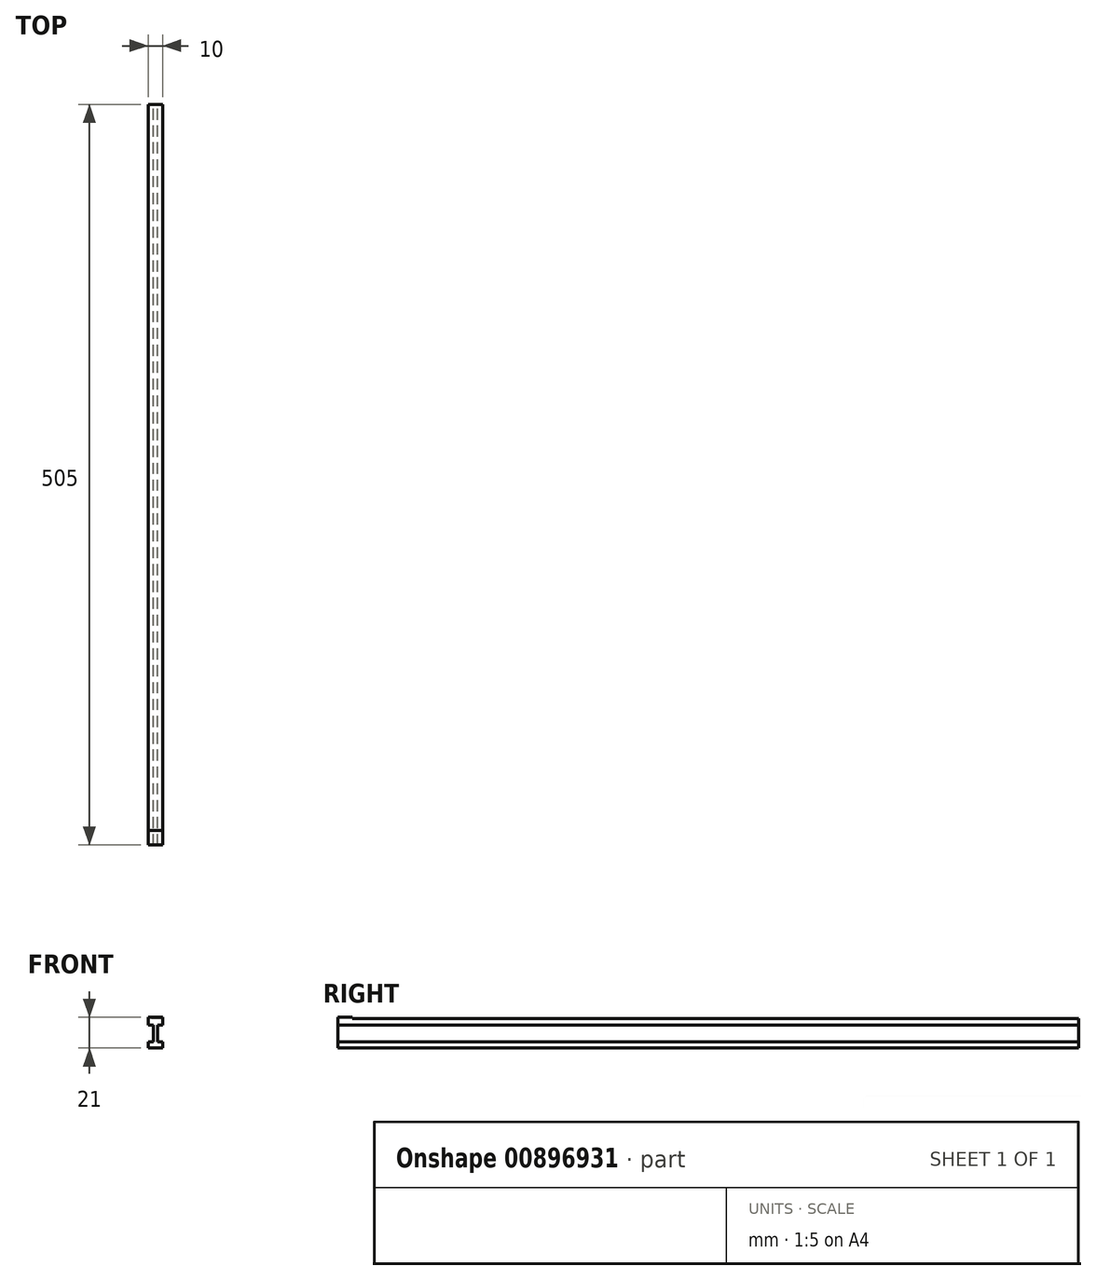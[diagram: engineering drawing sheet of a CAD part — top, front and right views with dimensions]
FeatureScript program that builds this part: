
annotation { "Feature Type Name" : "Feature", "Feature Type Description" : "" }
export const myFeature = defineFeature(function(context is Context, id is Id, definition is map)
    precondition{}
    {
        {
            var Q0;
            Q0=qCreatedBy(makeId("Front.planeOp"),FACE);
            var sketch = newSketch(context, id + "F0", { "sketchPlane" : qUnion([Q0])});
            skLineSegment(sketch, "E0.bottom", {"start": v(-5, 10) * mm, "end": v(5, 10) * mm});
            skLineSegment(sketch, "E0.top", {"start": v(-5, -10) * mm, "end": v(5, -10) * mm});
            skLineSegment(sketch, "E0.left", {"start": v(-5, 10) * mm, "end": v(-5, -10) * mm});
            skLineSegment(sketch, "E0.right", {"start": v(5, 10) * mm, "end": v(5, -10) * mm});
            skPoint(sketch, "E0.middle", {"position": v(0, 0) * mm});
            skLineSegment(sketch, "E1", {"start": v(5, -10) * mm, "end": v(5, -5.75) * mm});
            skPoint(sketch, "E2", {"position": v(-5, -5.75) * mm});
            skPoint(sketch, "E3", {"position": v(5, 5.75) * mm});
            skPoint(sketch, "E4", {"position": v(-5, 5.75) * mm});
            skPoint(sketch, "E5", {"position": v(1.5, 10) * mm});
            skPoint(sketch, "E6", {"position": v(-1.5, 10) * mm});
            skLineSegment(sketch, "E7.bottom", {"start": v(-1.5, 10) * mm, "end": v(1.5, 10) * mm});
            skLineSegment(sketch, "E7.top", {"start": v(-1.5, 10) * mm, "end": v(1.5, 10) * mm});
            skLineSegment(sketch, "E7.left", {"start": v(-1.5, 10) * mm, "end": v(-1.5, 10) * mm});
            skLineSegment(sketch, "E7.right", {"start": v(1.5, 10) * mm, "end": v(1.5, 10) * mm});
            skLineSegment(sketch, "E8.bottom", {"start": v(1.5, -10) * mm, "end": v(-1.5, -10) * mm});
            skLineSegment(sketch, "E8.top", {"start": v(1.5, 10) * mm, "end": v(-1.5, 10) * mm});
            skLineSegment(sketch, "E8.left", {"start": v(1.5, -10) * mm, "end": v(1.5, 10) * mm});
            skLineSegment(sketch, "E8.right", {"start": v(-1.5, -10) * mm, "end": v(-1.5, 10) * mm});
            skLineSegment(sketch, "E9.bottom", {"start": v(5, -5.75) * mm, "end": v(1.5, -5.75) * mm});
            skLineSegment(sketch, "E9.top", {"start": v(5, 5.75) * mm, "end": v(1.5, 5.75) * mm});
            skLineSegment(sketch, "E9.left", {"start": v(5, -5.75) * mm, "end": v(5, 5.75) * mm});
            skLineSegment(sketch, "E9.right", {"start": v(1.5, -5.75) * mm, "end": v(1.5, 5.75) * mm});
            skLineSegment(sketch, "E10.bottom", {"start": v(-5, 5.75) * mm, "end": v(-1.5, 5.75) * mm});
            skLineSegment(sketch, "E10.top", {"start": v(-5, -10) * mm, "end": v(-1.5, -10) * mm});
            skLineSegment(sketch, "E10.left", {"start": v(-5, 5.75) * mm, "end": v(-5, -10) * mm});
            skLineSegment(sketch, "E10.right", {"start": v(-1.5, 5.75) * mm, "end": v(-1.5, -10) * mm});
            skLineSegment(sketch, "E11.bottom", {"start": v(-5, -5.75) * mm, "end": v(-1.5, -5.75) * mm});
            skLineSegment(sketch, "E11.left", {"start": v(-5, -5.75) * mm, "end": v(-5, -10) * mm});
            skLineSegment(sketch, "E11.right", {"start": v(-1.5, -5.75) * mm, "end": v(-1.5, -10) * mm});
            skSolve(sketch);
        }
        {
            var Q0;
            {var subQ0=sQuery(id+"F0.wireOp",EDGE,"E8.left");var subQ1=sQuery(id+"F0.wireOp",EDGE,"E0.bottom");var subQ2=makeQuery(id+"F0.imprint","INTERSECT",VERTEX,{"derivedFrom":[subQ1,subQ0]});Q0=makeQuery(id+"F0.imprint","IMPRINT",FACE,{"disambiguationData":[TD([[makeQuery(id+"F0.imprint","IMPRINT",EDGE,{"disambiguationData":[TD([[subQ2,1.0]])],"derivedFrom":subQ1}),-1.0]])]});}
            var Q1;
            {var subQ5=sQuery(id+"F0.wireOp",EDGE,"E11.bottom");Q1=makeQuery(id+"F0.imprint","IMPRINT",FACE,{"disambiguationData":[TD([[makeQuery(id+"F0.imprint","IMPRINT",EDGE,{"derivedFrom":subQ5}),-1.0]])]});}
            var Q2;
            {var subQ5=sQuery(id+"F0.wireOp",EDGE,"E9.bottom");Q2=makeQuery(id+"F0.imprint","IMPRINT",FACE,{"disambiguationData":[TD([[makeQuery(id+"F0.imprint","IMPRINT",EDGE,{"derivedFrom":subQ5}),1.0]])]});}
            var Q3;
            {var subQ5=sQuery(id+"F0.wireOp",EDGE,"E9.top");Q3=makeQuery(id+"F0.imprint","IMPRINT",FACE,{"disambiguationData":[TD([[makeQuery(id+"F0.imprint","IMPRINT",EDGE,{"derivedFrom":subQ5}),-1.0]])]});}
            var Q4;
            {var subQ5=sQuery(id+"F0.wireOp",EDGE,"E10.bottom");Q4=makeQuery(id+"F0.imprint","IMPRINT",FACE,{"disambiguationData":[TD([[makeQuery(id+"F0.imprint","IMPRINT",EDGE,{"derivedFrom":subQ5}),1.0]])]});}
            extrude(context, id + "F1", {"entities" : qUnion([Q0, Q1, Q2, Q3, Q4]), "depth" : 505 * mm, "offsetDistance" : 25 * mm});
        }
        {
            var Q0;
            Q0=makeQuery(id+"F1.opExtrude","SWEPT_FACE",FACE,{"disambiguationData":[OSD([sQuery(id+"F0.wireOp",EDGE,"E0.bottom")])]});
            var sketch = newSketch(context, id + "F2", { "sketchPlane" : qUnion([Q0])});
            skLineSegment(sketch, "E12.bottom", {"start": v(5, 0) * mm, "end": v(-5, 0) * mm});
            skLineSegment(sketch, "E12.top", {"start": v(5, -495) * mm, "end": v(-5, -495) * mm});
            skLineSegment(sketch, "E12.left", {"start": v(5, 0) * mm, "end": v(5, -495) * mm});
            skLineSegment(sketch, "E12.right", {"start": v(-5, 0) * mm, "end": v(-5, -495) * mm});
            skLineSegment(sketch, "E13.top", {"start": v(5, -505) * mm, "end": v(-5, -505) * mm});
            skLineSegment(sketch, "E13.left", {"start": v(5, -495) * mm, "end": v(5, -505) * mm});
            skLineSegment(sketch, "E13.right", {"start": v(-5, -495) * mm, "end": v(-5, -505) * mm});
            skSolve(sketch);
        }
        {
            var Q0;
            Q0=makeQuery(id+"F2.imprint","IMPRINT",FACE,{"disambiguationData":[TD([[makeQuery(id+"F2.imprint","IMPRINT",EDGE,{"derivedFrom":sQuery(id+"F2.wireOp",EDGE,"E12.top")}),1.0]])]});
            extrude(context, id + "F3", {"entities" : qUnion([Q0]), "operationType" : NewBodyOperationType.ADD, "depth" : 1 * mm, "offsetDistance" : 25 * mm});
        }
    });
